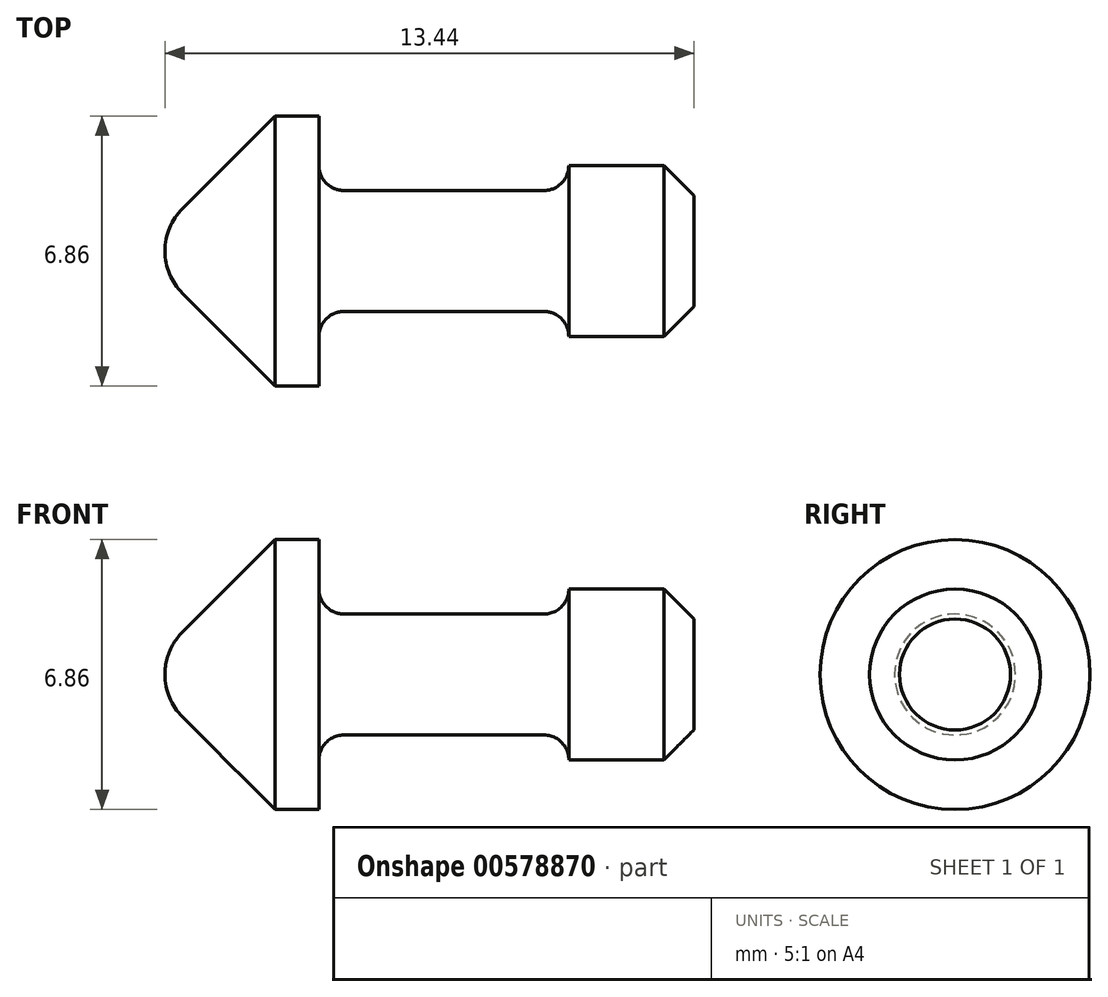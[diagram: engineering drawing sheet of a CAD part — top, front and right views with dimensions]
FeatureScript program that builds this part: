
annotation { "Feature Type Name" : "Feature", "Feature Type Description" : "" }
export const myFeature = defineFeature(function(context is Context, id is Id, definition is map)
    precondition{}
    {
        {
            var Q0;
            Q0=qCreatedBy(makeId("Right.planeOp"),FACE);
            var sketch = newSketch(context, id + "F0", { "sketchPlane" : qUnion([Q0])});
            skCircle(sketch, "E0", {"center": v(0, 0) * mm, "radius": 2.17 * mm});
            skCircle(sketch, "E1", {"center": v(0, 0) * mm, "radius": 3.43 * mm});
            skSolve(sketch);
        }
        {
            var Q0;
            Q0=makeQuery(id+"F0.imprint","IMPRINT",FACE,{"disambiguationData":[TD([[makeQuery(id+"F0.imprint","IMPRINT",EDGE,{"derivedFrom":sQuery(id+"F0.wireOp",EDGE,"E0")}),1.0]])]});
            extrude(context, id + "F1", {"entities" : qUnion([Q0]), "depth" : 9.52 * mm});
        }
        {
            var Q0;
            Q0=makeQuery(id+"F0.imprint","IMPRINT",FACE,{"disambiguationData":[TD([[makeQuery(id+"F0.imprint","IMPRINT",EDGE,{"derivedFrom":sQuery(id+"F0.wireOp",EDGE,"E0")}),-1.0]])]});
            var Q1;
            Q1=makeQuery(id+"F0.imprint","IMPRINT",FACE,{"disambiguationData":[TD([[makeQuery(id+"F0.imprint","IMPRINT",EDGE,{"derivedFrom":sQuery(id+"F0.wireOp",EDGE,"E0")}),1.0]])]});
            extrude(context, id + "F2", {"entities" : qUnion([Q0, Q1]), "operationType" : NewBodyOperationType.ADD, "oppositeDirection" : true, "depth" : 3.94 * mm});
        }
        {
            var Q0;
            Q0=qCreatedBy(makeId("Front.planeOp"),FACE);
            var sketch = newSketch(context, id + "F3", { "sketchPlane" : qUnion([Q0])});
            skLineSegment(sketch, "E2", {"start": v(0, 2.17) * mm, "end": v(6.35, 2.17) * mm});
            skLineSegment(sketch, "E3", {"start": v(0.64, 1.54) * mm, "end": v(5.72, 1.54) * mm});
            skLineSegment(sketch, "E4", {"start": v(6.35, 2.17) * mm, "end": v(6.35, 2.17) * mm});
            skPoint(sketch, "E5.0.end.orphan", {"position": v(9.53, -2.17) * mm});
            skPoint(sketch, "E5.0.start.orphan", {"position": v(9.53, 2.17) * mm});
            skLineSegment(sketch, "E6", {"start": v(0, 2.17) * mm, "end": v(0, 2.17) * mm});
            skPoint(sketch, "E7.visualSharp", {"position": v(6.35, 1.54) * mm});
            skArc(sketch, "E7.filletArc", {"start": v(5.72, 1.54) * mm, "mid": v(6.16, 1.72) * mm, "end": v(6.35, 2.17) * mm});
            skPoint(sketch, "E8.visualSharp", {"position": v(0, 1.54) * mm});
            skArc(sketch, "E8.filletArc", {"start": v(0, 2.17) * mm, "mid": v(0.19, 1.72) * mm, "end": v(0.64, 1.54) * mm});
            skLineSegment(sketch, "E9", {"start": v(-1.38, 0) * mm, "end": v(8.16, 0) * mm, "construction": true});
            skSolve(sketch);
        }
        {
            var Q0;
            Q0=makeQuery(id+"F3.imprint","IMPRINT",FACE,{"disambiguationData":[TD([[makeQuery(id+"F3.imprint","IMPRINT",EDGE,{"derivedFrom":sQuery(id+"F3.wireOp",EDGE,"E2")}),-1.0]])]});
            var Q1;
            Q1=sQuery(id+"F3.wireOp",EDGE,"E9");
            revolve(context, id + "F4", {"operationType" : NewBodyOperationType.REMOVE, "entities" : qUnion([Q0]), "axis" : qUnion([Q1]), "revolveType" : RevolveType.FULL, "oppositeDirection" : true});
        }
        {
            var Q0;
            Q0=makeQuery(id+"F1.opExtrude","CAP_EDGE",EDGE,{"disambiguationData":[OSD([sQuery(id+"F0.wireOp",EDGE,"E0")])],"isStart":false});
            chamfer(context, id + "F5", {"entities" : qUnion([Q0]), "width" : 0.76 * mm, "tangentPropagation" : true});
        }
        {
            var Q0;
            Q0=qCreatedBy(makeId("Front.planeOp"),FACE);
            var sketch = newSketch(context, id + "F6", { "sketchPlane" : qUnion([Q0])});
            skLineSegment(sketch, "E10.0", {"start": v(0, 3.43) * mm, "end": v(0, -3.43) * mm});
            skLineSegment(sketch, "E11", {"start": v(-3.94, 3.43) * mm, "end": v(-1.11, 3.43) * mm});
            skLineSegment(sketch, "E12", {"start": v(-1.11, -3.43) * mm, "end": v(-3.94, -3.43) * mm});
            skLineSegment(sketch, "E13", {"start": v(-3.47, 1.08) * mm, "end": v(-1.11, 3.43) * mm});
            skLineSegment(sketch, "E14", {"start": v(-3.47, -1.08) * mm, "end": v(-1.11, -3.43) * mm});
            skLineSegment(sketch, "E15.0", {"start": v(-3.94, 3.43) * mm, "end": v(-3.94, -3.43) * mm});
            skArc(sketch, "E16", {"start": v(-3.47, 1.08) * mm, "mid": v(-3.91, 0) * mm, "end": v(-3.47, -1.08) * mm});
            skLineSegment(sketch, "E17", {"start": v(0, 0) * mm, "end": v(-3.94, 0) * mm, "construction": true});
            skPoint(sketch, "E18.orphan", {"position": v(-4.54, 0) * mm});
            skLineSegment(sketch, "E19", {"start": v(-3.94, 0) * mm, "end": v(-3.91, 0) * mm});
            skSolve(sketch);
        }
        {
            var Q0;
            {var subQ0=sQuery(id+"F6.wireOp",EDGE,"E11");Q0=makeQuery(id+"F6.imprint","IMPRINT",FACE,{"disambiguationData":[TD([[makeQuery(id+"F6.imprint","IMPRINT",EDGE,{"derivedFrom":subQ0}),-1.0]])]});}
            var Q1;
            Q1=sQuery(id+"F6.wireOp",EDGE,"E19");
            revolve(context, id + "F7", {"operationType" : NewBodyOperationType.REMOVE, "entities" : qUnion([Q0]), "axis" : qUnion([Q1]), "revolveType" : RevolveType.FULL, "oppositeDirection" : true});
        }
    });
